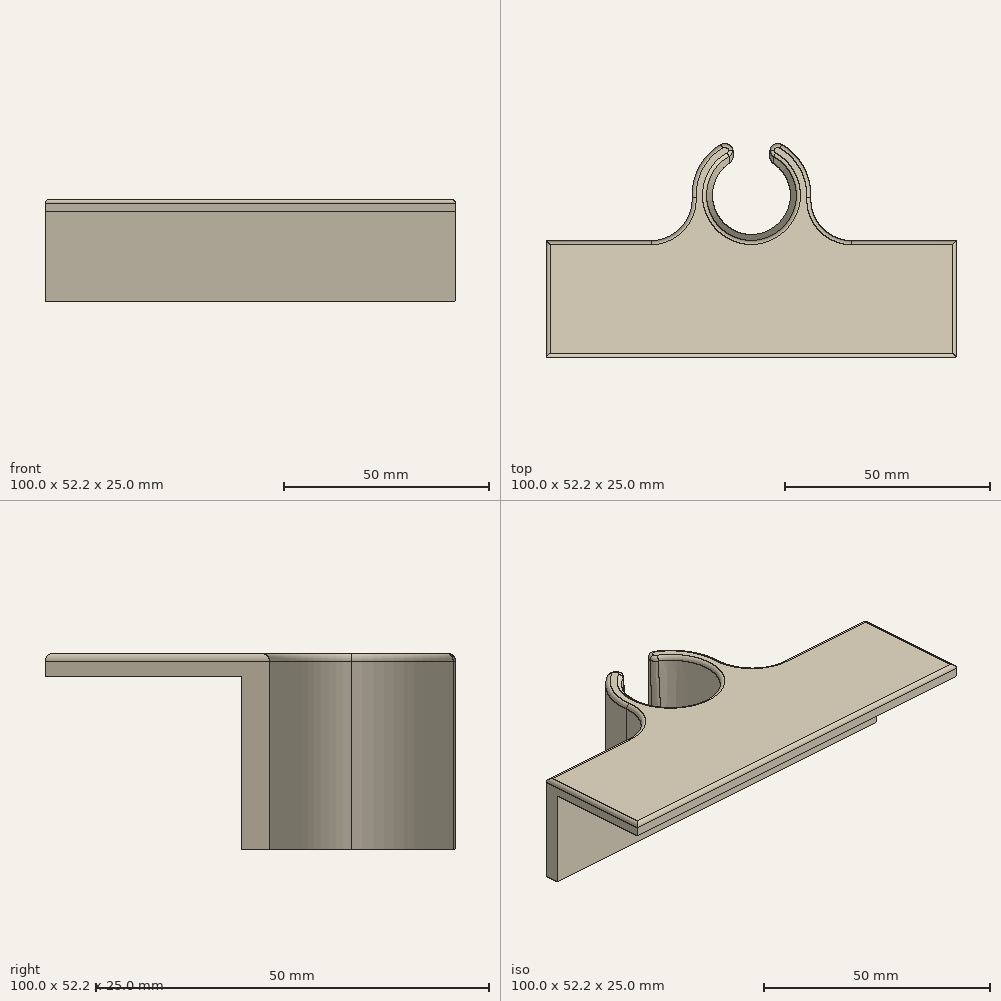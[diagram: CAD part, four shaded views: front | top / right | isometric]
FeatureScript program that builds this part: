
annotation { "Feature Type Name" : "Feature", "Feature Type Description" : "" }
export const myFeature = defineFeature(function(context is Context, id is Id, definition is map)
    precondition{}
    {
        {
            var Q0;
            Q0=qCreatedBy(makeId("Front.planeOp"),FACE);
            var sketch = newSketch(context, id + "F0", { "sketchPlane" : qUnion([Q0])});
            skLineSegment(sketch, "E0", {"start": v(-14.5, 12.5) * mm, "end": v(-14.5, -12.5) * mm});
            skLineSegment(sketch, "E1", {"start": v(-14.5, -12.5) * mm, "end": v(-9.5, -12.5) * mm});
            skLineSegment(sketch, "E2", {"start": v(-9.5, -12.5) * mm, "end": v(-11, 12.5) * mm});
            skLineSegment(sketch, "E3", {"start": v(-11, 12.5) * mm, "end": v(-14.5, 12.5) * mm});
            skLineSegment(sketch, "E4", {"start": v(0, 50) * mm, "end": v(0, -70) * mm});
            skSolve(sketch);
        }
        {
            var Q0;
            Q0=makeQuery(id+"F0.imprint","IMPRINT",FACE,{"disambiguationData":[TD([[makeQuery(id+"F0.imprint","IMPRINT",EDGE,{"derivedFrom":sQuery(id+"F0.wireOp",EDGE,"E0")}),1.0]])]});
            var Q1;
            Q1=sQuery(id+"F0.wireOp",EDGE,"E4");
            revolve(context, id + "F1", {"entities" : qUnion([Q0]), "axis" : qUnion([Q1]), "revolveType" : RevolveType.FULL});
        }
        {
            var Q0;
            Q0=qCreatedBy(makeId("Top.planeOp"),FACE);
            var sketch = newSketch(context, id + "F2", { "sketchPlane" : qUnion([Q0])});
            skLineSegment(sketch, "E5.bottom", {"start": v(50, -11) * mm, "end": v(-50, -11) * mm});
            skLineSegment(sketch, "E5.top", {"start": v(50, -14.5) * mm, "end": v(-50, -14.5) * mm});
            skLineSegment(sketch, "E5.left", {"start": v(50, -11) * mm, "end": v(50, -14.5) * mm});
            skLineSegment(sketch, "E5.right", {"start": v(-50, -11) * mm, "end": v(-50, -14.5) * mm});
            skPoint(sketch, "E5.middle", {"position": v(0, -12.75) * mm});
            skSolve(sketch);
        }
        {
            var Q0;
            Q0=makeQuery(id+"F2.imprint","IMPRINT",FACE,{"disambiguationData":[TD([[makeQuery(id+"F2.imprint","IMPRINT",EDGE,{"derivedFrom":sQuery(id+"F2.wireOp",EDGE,"E5.bottom")}),1.0]])]});
            var Q1;
            Q1=makeQuery(id+"F1.opRevolve","SWEPT_FACE",FACE,{"disambiguationData":[OSD([sQuery(id+"F0.wireOp",EDGE,"E3")])]});
            var Q2;
            Q2=makeQuery(id+"F1.opRevolve","SWEPT_FACE",FACE,{"disambiguationData":[OSD([sQuery(id+"F0.wireOp",EDGE,"E1")])]});
            extrude(context, id + "F3", {"entities" : qUnion([Q0]), "operationType" : NewBodyOperationType.ADD, "endBound" : BoundingType.UP_TO_SURFACE, "endBoundEntityFace" : qUnion([Q1]), "depth" : 40 * mm, "hasSecondDirection" : true, "secondDirectionBound" : SecondDirectionBoundingType.UP_TO_SURFACE, "secondDirectionOppositeDirection" : true, "secondDirectionBoundEntityFace" : qUnion([Q2]), "secondDirectionDepth" : 12.5 * mm});
        }
        {
            var Q0;
            Q0=qCreatedBy(makeId("Top.planeOp"),FACE);
            var sketch = newSketch(context, id + "F4", { "sketchPlane" : qUnion([Q0])});
            skLineSegment(sketch, "E6.bottom", {"start": v(4.48, 2.08) * mm, "end": v(-4.48, 2.08) * mm});
            skLineSegment(sketch, "E6.top", {"start": v(4.48, 44.45) * mm, "end": v(-4.48, 44.45) * mm});
            skLineSegment(sketch, "E6.left", {"start": v(4.48, 2.08) * mm, "end": v(4.48, 44.45) * mm});
            skLineSegment(sketch, "E6.right", {"start": v(-4.48, 2.08) * mm, "end": v(-4.48, 44.45) * mm});
            skPoint(sketch, "E6.middle", {"position": v(0, 23.26) * mm});
            skSolve(sketch);
        }
        {
            var Q0;
            Q0 = qSketchRegion(id + "F4", true);
            extrude(context, id + "F5", {"entities" : qUnion([Q0]), "operationType" : NewBodyOperationType.REMOVE, "endBound" : BoundingType.SYMMETRIC, "oppositeDirection" : true, "depth" : 50 * mm});
        }
        {
            var Q0;
            Q0=makeQuery(id+"F3.boolean.opBoolean","INTERSECT",EDGE,{"disambiguationData":[OD(1.0)],"derivedFrom":[makeQuery(id+"F1.opRevolve","SWEPT_FACE",FACE,{"disambiguationData":[OSD([sQuery(id+"F0.wireOp",EDGE,"E0")])]}),makeQuery(id+"F3.opExtrude","SWEPT_FACE",FACE,{"disambiguationData":[OSD([sQuery(id+"F2.wireOp",EDGE,"E5.bottom")])]})]});
            var Q1;
            Q1=makeQuery(id+"F3.boolean.opBoolean","INTERSECT",EDGE,{"disambiguationData":[OD(0.0)],"derivedFrom":[makeQuery(id+"F1.opRevolve","SWEPT_FACE",FACE,{"disambiguationData":[OSD([sQuery(id+"F0.wireOp",EDGE,"E0")])]}),makeQuery(id+"F3.opExtrude","SWEPT_FACE",FACE,{"disambiguationData":[OSD([sQuery(id+"F2.wireOp",EDGE,"E5.bottom")])]})]});
            fillet(context, id + "F6", {"entities" : qUnion([Q0, Q1]), "radius" : 10 * mm, "tangentPropagation" : true, "allowEdgeOverflow" : false});
        }
        {
            var Q0;
            Q0=makeQuery(id+"F5.boolean.opBoolean","INTERSECT",EDGE,{"derivedFrom":[makeQuery(id+"F1.opRevolve","SWEPT_FACE",FACE,{"disambiguationData":[OSD([sQuery(id+"F0.wireOp",EDGE,"E2")])]}),makeQuery(id+"F5.opExtrude","SWEPT_FACE",FACE,{"disambiguationData":[OSD([sQuery(id+"F4.wireOp",EDGE,"E6.left")])]})]});
            var Q1;
            Q1=makeQuery(id+"F5.boolean.opBoolean","INTERSECT",EDGE,{"derivedFrom":[makeQuery(id+"F1.opRevolve","SWEPT_FACE",FACE,{"disambiguationData":[OSD([sQuery(id+"F0.wireOp",EDGE,"E0")])]}),makeQuery(id+"F5.opExtrude","SWEPT_FACE",FACE,{"disambiguationData":[OSD([sQuery(id+"F4.wireOp",EDGE,"E6.left")])]})]});
            var Q2;
            Q2=makeQuery(id+"F5.boolean.opBoolean","INTERSECT",EDGE,{"derivedFrom":[makeQuery(id+"F1.opRevolve","SWEPT_FACE",FACE,{"disambiguationData":[OSD([sQuery(id+"F0.wireOp",EDGE,"E0")])]}),makeQuery(id+"F5.opExtrude","SWEPT_FACE",FACE,{"disambiguationData":[OSD([sQuery(id+"F4.wireOp",EDGE,"E6.right")])]})]});
            var Q3;
            Q3=makeQuery(id+"F5.boolean.opBoolean","INTERSECT",EDGE,{"derivedFrom":[makeQuery(id+"F1.opRevolve","SWEPT_FACE",FACE,{"disambiguationData":[OSD([sQuery(id+"F0.wireOp",EDGE,"E2")])]}),makeQuery(id+"F5.opExtrude","SWEPT_FACE",FACE,{"disambiguationData":[OSD([sQuery(id+"F4.wireOp",EDGE,"E6.right")])]})]});
            fillet(context, id + "F7", {"entities" : qUnion([Q0, Q1, Q2, Q3]), "radius" : 2 * mm, "tangentPropagation" : true, "allowEdgeOverflow" : false});
        }
        {
            var Q0;
            Q0=makeQuery(id+"F3.opExtrude","SWEPT_FACE",FACE,{"disambiguationData":[OSD([sQuery(id+"F2.wireOp",EDGE,"E5.top")])]});
            var sketch = newSketch(context, id + "F8", { "sketchPlane" : qUnion([Q0])});
            skLineSegment(sketch, "E7.bottom", {"start": v(50, 9.5) * mm, "end": v(-50, 9.5) * mm});
            skLineSegment(sketch, "E7.top", {"start": v(50, 12.5) * mm, "end": v(-50, 12.5) * mm});
            skLineSegment(sketch, "E7.left", {"start": v(50, 9.5) * mm, "end": v(50, 12.5) * mm});
            skLineSegment(sketch, "E7.right", {"start": v(-50, 9.5) * mm, "end": v(-50, 12.5) * mm});
            skPoint(sketch, "E7.middle", {"position": v(0, 11) * mm});
            skSolve(sketch);
        }
        {
            var Q0;
            Q0=makeQuery(id+"F8.imprint","IMPRINT",FACE,{"disambiguationData":[TD([[makeQuery(id+"F8.imprint","IMPRINT",EDGE,{"derivedFrom":sQuery(id+"F8.wireOp",EDGE,"E7.bottom")}),-1.0]])]});
            extrude(context, id + "F9", {"entities" : qUnion([Q0]), "operationType" : NewBodyOperationType.ADD, "depth" : 25 * mm});
        }
        {
            var Q0;
            {var subQ0=sQuery(id+"F0.wireOp",EDGE,"E3");Q0=makeQuery(id+"F9.boolean.opBoolean","MERGE",FACE,{"derivedFrom":[makeQuery(id+"F3.boolean.opBoolean","MERGE",FACE,{"derivedFrom":[makeQuery(id+"F1.opRevolve","SWEPT_FACE",FACE,{"disambiguationData":[OSD([subQ0])]}),makeQuery(id+"F3.opExtrude","CAP_FACE",FACE,{"disambiguationData":[OSD([subQ0])],"isStart":false})]}),makeQuery(id+"F9.opExtrude","SWEPT_FACE",FACE,{"disambiguationData":[OSD([sQuery(id+"F8.wireOp",EDGE,"E7.top")])]})]});}
            var Q1;
            Q1=makeQuery(id+"F3.opExtrude","TWEAK_EDGE",EDGE,{"derivedFrom":[makeQuery(id+"F2.imprint","IMPRINT",EDGE,{"derivedFrom":sQuery(id+"F2.wireOp",EDGE,"E5.bottom")}),makeQuery(id+"F2.imprint","IMPRINT",EDGE,{"derivedFrom":sQuery(id+"F2.wireOp",EDGE,"E5.right")})]});
            var Q2;
            Q2=makeQuery(id+"F3.opExtrude","TWEAK_EDGE",EDGE,{"derivedFrom":[makeQuery(id+"F2.imprint","IMPRINT",EDGE,{"derivedFrom":sQuery(id+"F2.wireOp",EDGE,"E5.bottom")}),makeQuery(id+"F2.imprint","IMPRINT",EDGE,{"derivedFrom":sQuery(id+"F2.wireOp",EDGE,"E5.left")})]});
            fillet(context, id + "F10", {"entities" : qUnion([Q0, Q1, Q2]), "radius" : 1 * mm, "tangentPropagation" : true, "allowEdgeOverflow" : false});
        }
    });
